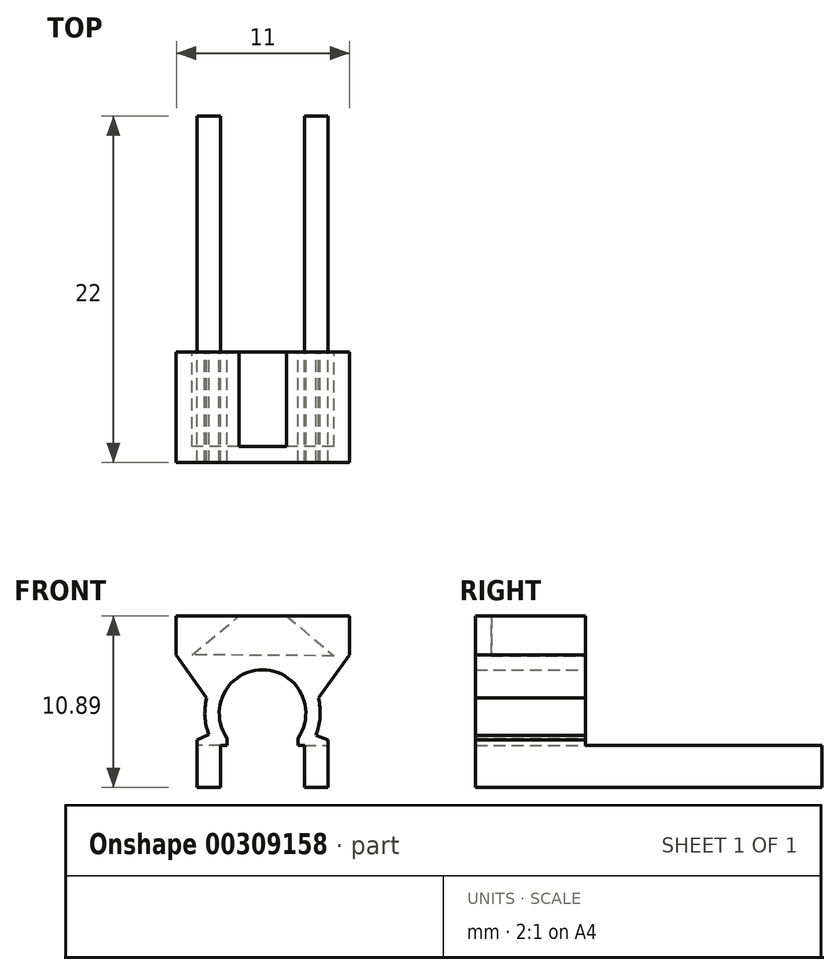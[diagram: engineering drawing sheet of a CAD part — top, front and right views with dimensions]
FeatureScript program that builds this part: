
annotation { "Feature Type Name" : "Feature", "Feature Type Description" : "" }
export const myFeature = defineFeature(function(context is Context, id is Id, definition is map)
    precondition{}
    {
        {
            var Q0;
            Q0=qCreatedBy(makeId("Front.planeOp"),FACE);
            var sketch = newSketch(context, id + "F0", { "sketchPlane" : qUnion([Q0])});
            skLineSegment(sketch, "E0", {"start": v(-3.34, -1.58) * mm, "end": v(-3.32, -1.6) * mm});
            skArc(sketch, "E1.trimOffspring", {"start": v(3.45, -1.63) * mm, "mid": v(0.1, 3.44) * mm, "end": v(-3.34, -1.58) * mm});
            skLineSegment(sketch, "E2", {"start": v(-3.32, -1.6) * mm, "end": v(-3.32, -2.28) * mm});
            skLineSegment(sketch, "E3", {"start": v(-3.32, -4.95) * mm, "end": v(-2.59, -4.95) * mm});
            skLineSegment(sketch, "E4", {"start": v(3.45, -1.63) * mm, "end": v(3.45, -2.28) * mm});
            skLineSegment(sketch, "E5", {"start": v(3.45, -4.95) * mm, "end": v(2.72, -4.95) * mm});
            skLineSegment(sketch, "E6", {"start": v(-4.09, -1.94) * mm, "end": v(-4.09, -4.95) * mm});
            skLineSegment(sketch, "E7", {"start": v(-4.09, -4.95) * mm, "end": v(-3.32, -4.95) * mm});
            skLineSegment(sketch, "E8.MirrorCS", {"start": v(4.22, -1.94) * mm, "end": v(4.22, -4.95) * mm});
            skLineSegment(sketch, "E9.MirrorCS", {"start": v(4.22, -4.95) * mm, "end": v(3.45, -4.95) * mm});
            skLineSegment(sketch, "E10", {"start": v(-4.09, -1.94) * mm, "end": v(-3.32, -1.6) * mm});
            skLineSegment(sketch, "E11", {"start": v(4.22, -1.94) * mm, "end": v(3.45, -1.63) * mm});
            skLineSegment(sketch, "E12", {"start": v(0.1, 3.44) * mm, "end": v(-4.4, 3.47) * mm});
            skLineSegment(sketch, "E13", {"start": v(0.1, 3.44) * mm, "end": v(4.6, 3.4) * mm});
            skLineSegment(sketch, "E14", {"start": v(0.1, 3.44) * mm, "end": v(0.1, 5.94) * mm, "construction": true});
            skLineSegment(sketch, "E15", {"start": v(-4.4, 3.47) * mm, "end": v(-1.41, 5.94) * mm});
            skLineSegment(sketch, "E16", {"start": v(1.6, 5.94) * mm, "end": v(4.6, 3.4) * mm});
            skLineSegment(sketch, "E17", {"start": v(-1.41, 5.94) * mm, "end": v(-5.41, 5.94) * mm});
            skLineSegment(sketch, "E18", {"start": v(-5.41, 5.94) * mm, "end": v(-5.41, 3.47) * mm});
            skLineSegment(sketch, "E19", {"start": v(-5.41, 3.47) * mm, "end": v(-3.48, 0.72) * mm});
            skLineSegment(sketch, "E20", {"start": v(1.6, 5.94) * mm, "end": v(5.59, 5.94) * mm});
            skLineSegment(sketch, "E21", {"start": v(5.59, 5.94) * mm, "end": v(5.59, 3.47) * mm});
            skLineSegment(sketch, "E22", {"start": v(5.59, 3.47) * mm, "end": v(3.6, 0.72) * mm});
            skLineSegment(sketch, "E23", {"start": v(-1.41, 5.94) * mm, "end": v(1.6, 5.94) * mm});
            skLineSegment(sketch, "E24", {"start": v(-3.32, -2.28) * mm, "end": v(-4.09, -2.28) * mm});
            skLineSegment(sketch, "E25", {"start": v(3.45, -2.28) * mm, "end": v(4.22, -2.28) * mm});
            skLineSegment(sketch, "E26", {"start": v(3.45, -2.28) * mm, "end": v(3.45, -4.95) * mm, "construction": true});
            skLineSegment(sketch, "E27.0", {"start": v(2.72, -2.28) * mm, "end": v(2.72, -4.95) * mm});
            skLineSegment(sketch, "E28.0", {"start": v(-2.59, -2.28) * mm, "end": v(-2.59, -4.95) * mm});
            skLineSegment(sketch, "E29", {"start": v(-2.59, -2.28) * mm, "end": v(-3.32, -2.28) * mm});
            skLineSegment(sketch, "E30", {"start": v(2.72, -2.28) * mm, "end": v(3.45, -2.28) * mm});
            skArc(sketch, "E31", {"start": v(2.3, -1.82) * mm, "mid": v(0.06, 2.52) * mm, "end": v(-2.18, -1.82) * mm});
            skLineSegment(sketch, "E32", {"start": v(2.72, -2.28) * mm, "end": v(2.3, -2.28) * mm});
            skLineSegment(sketch, "E33", {"start": v(-2.59, -2.28) * mm, "end": v(-2.18, -2.28) * mm});
            skLineSegment(sketch, "E34", {"start": v(2.3, -2.28) * mm, "end": v(2.3, -1.82) * mm});
            skLineSegment(sketch, "E35", {"start": v(-2.18, -2.28) * mm, "end": v(-2.18, -1.82) * mm});
            skPoint(sketch, "E36.orphan", {"position": v(-1.76, -2.28) * mm});
            skPoint(sketch, "E37.orphan", {"position": v(1.9, -2.28) * mm});
            skSolve(sketch);
        }
        {
            var Q0;
            Q0 = qSketchRegion(id + "F0", true);
            extrude(context, id + "F1", {"entities" : qUnion([Q0]), "depth" : 7 * mm});
        }
        {
            var Q0;
            Q0=makeQuery(id+"F0.imprint","IMPRINT",FACE,{"disambiguationData":[TD([[makeQuery(id+"F0.imprint","IMPRINT",EDGE,{"derivedFrom":sQuery(id+"F0.wireOp",EDGE,"E12")}),-1.0]])]});
            extrude(context, id + "F2", {"entities" : qUnion([Q0]), "operationType" : NewBodyOperationType.REMOVE, "depth" : 6 * mm, "offsetDistance" : 25 * mm});
        }
        {
            var Q0;
            Q0=makeQuery(id+"F0.imprint","IMPRINT",FACE,{"disambiguationData":[TD([[makeQuery(id+"F0.imprint","IMPRINT",EDGE,{"derivedFrom":sQuery(id+"F0.wireOp",EDGE,"E5")}),-1.0]])]});
            var Q1;
            Q1=makeQuery(id+"F0.imprint","IMPRINT",FACE,{"disambiguationData":[TD([[makeQuery(id+"F0.imprint","IMPRINT",EDGE,{"derivedFrom":sQuery(id+"F0.wireOp",EDGE,"E3")}),1.0]])]});
            extrude(context, id + "F3", {"entities" : qUnion([Q0, Q1]), "operationType" : NewBodyOperationType.ADD, "oppositeDirection" : true, "depth" : 15 * mm, "offsetDistance" : 25 * mm});
        }
    });
